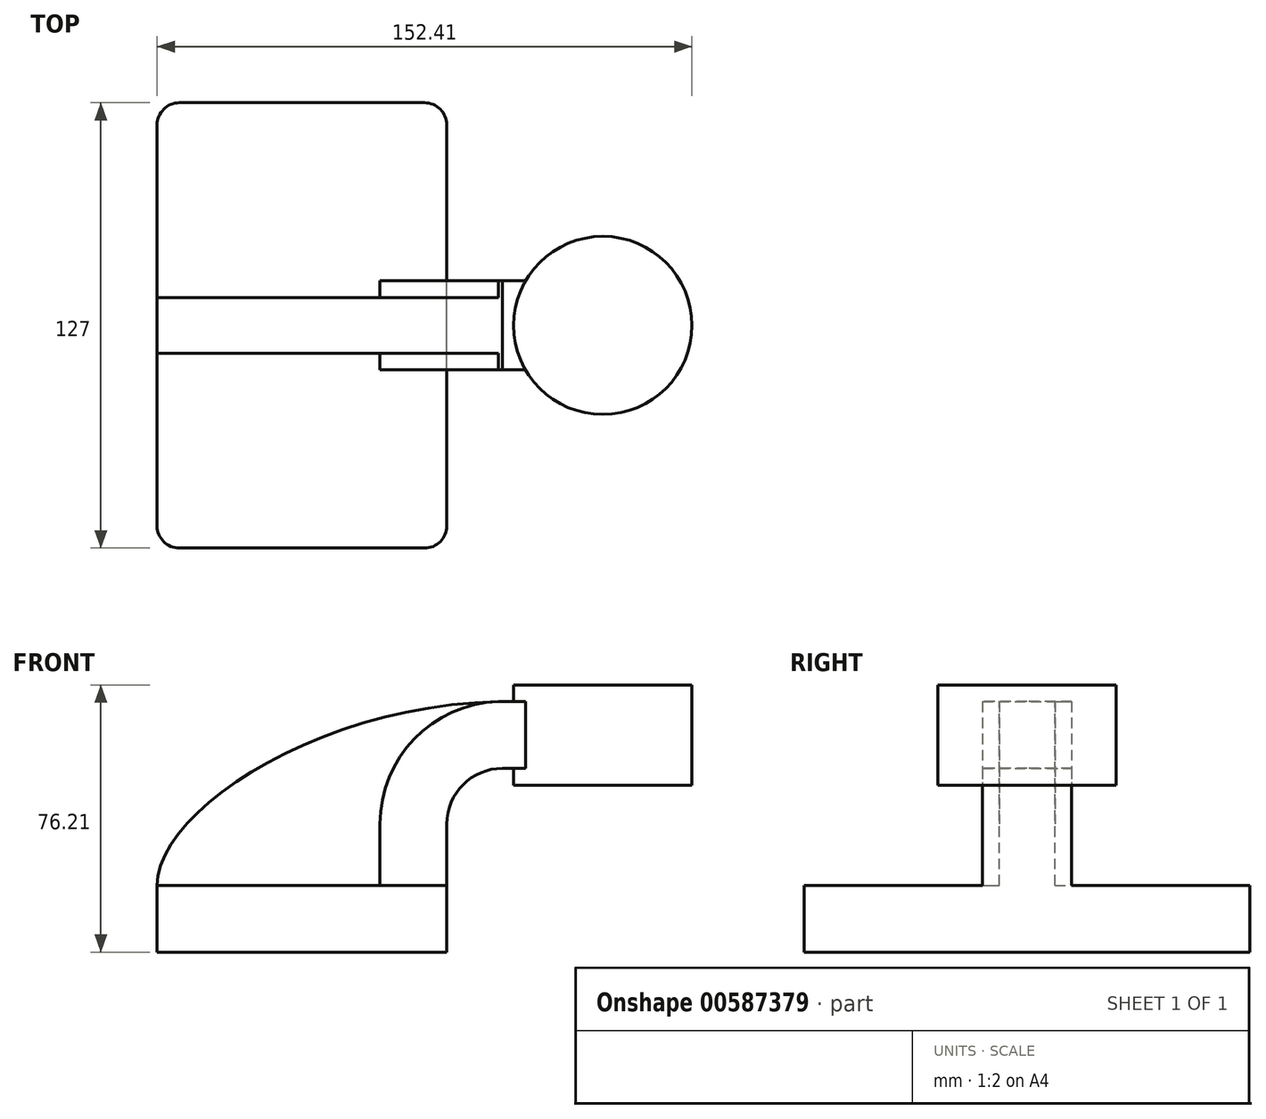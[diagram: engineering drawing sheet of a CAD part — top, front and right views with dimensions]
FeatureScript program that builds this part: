
annotation { "Feature Type Name" : "Feature", "Feature Type Description" : "" }
export const myFeature = defineFeature(function(context is Context, id is Id, definition is map)
    precondition{}
    {
        {
            var Q0;
            Q0=qCreatedBy(makeId("Front.planeOp"),FACE);
            var sketch = newSketch(context, id + "F0", { "sketchPlane" : qUnion([Q0])});
            skLineSegment(sketch, "E0.bottom", {"start": v(41.27, 9.53) * mm, "end": v(-41.28, 9.53) * mm});
            skLineSegment(sketch, "E0.top", {"start": v(41.28, -9.52) * mm, "end": v(-41.27, -9.52) * mm});
            skLineSegment(sketch, "E0.left", {"start": v(41.28, 9.53) * mm, "end": v(41.28, -9.52) * mm});
            skLineSegment(sketch, "E0.right", {"start": v(-41.28, 9.53) * mm, "end": v(-41.28, -9.52) * mm});
            skPoint(sketch, "E0.middle", {"position": v(0, 0) * mm});
            skLineSegment(sketch, "E1.bottom", {"start": v(60.33, 38.1) * mm, "end": v(111.12, 38.1) * mm});
            skLineSegment(sketch, "E1.top", {"start": v(60.32, 66.68) * mm, "end": v(111.12, 66.68) * mm});
            skLineSegment(sketch, "E1.left", {"start": v(60.33, 38.1) * mm, "end": v(60.32, 66.68) * mm});
            skLineSegment(sketch, "E1.right", {"start": v(111.12, 38.1) * mm, "end": v(111.12, 66.68) * mm});
            skLineSegment(sketch, "E2", {"start": v(41.27, 9.53) * mm, "end": v(41.27, 27) * mm});
            skArc(sketch, "E3", {"start": v(41.27, 27) * mm, "mid": v(45.92, 38.23) * mm, "end": v(57.15, 42.88) * mm});
            skLineSegment(sketch, "E4", {"start": v(57.15, 42.88) * mm, "end": v(85.72, 42.88) * mm});
            skPoint(sketch, "E4.endSnap0", {"position": v(85.72, 38.1) * mm});
            skLineSegment(sketch, "E5.0", {"start": v(57.15, 61.93) * mm, "end": v(85.72, 61.93) * mm});
            skArc(sketch, "E5.1", {"start": v(22.22, 27) * mm, "mid": v(32.45, 51.7) * mm, "end": v(57.15, 61.93) * mm});
            skLineSegment(sketch, "E5.2", {"start": v(22.22, 9.53) * mm, "end": v(22.22, 27) * mm});
            skLineSegment(sketch, "E6", {"start": v(85.72, 38.1) * mm, "end": v(85.72, 66.68) * mm});
            skFitSpline(sketch, "E7", {"points": [v(-41.28, 9.52) * mm, v(57.15, 61.93) * mm], "startDerivative": vector(-0.01, 63.76) * mm, "endDerivative": vector(156.94, 2.03) * mm});
            skSolve(sketch);
        }
        {
            var Q0;
            Q0=makeQuery(id+"F0.imprint","IMPRINT",FACE,{"disambiguationData":[TD([[makeQuery(id+"F0.imprint","IMPRINT",EDGE,{"derivedFrom":sQuery(id+"F0.wireOp",EDGE,"E0.top")}),-1.0]])]});
            extrude(context, id + "F1", {"entities" : qUnion([Q0]), "endBound" : BoundingType.SYMMETRIC, "depth" : 127 * mm, "offsetDistance" : 25.4 * mm});
        }
        {
            var Q0;
            {var subQ1=sQuery(id+"F0.wireOp",EDGE,"E2");Q0=makeQuery(id+"F0.imprint","IMPRINT",FACE,{"disambiguationData":[TD([[makeQuery(id+"F0.imprint","IMPRINT",EDGE,{"derivedFrom":subQ1}),1.0]])]});}
            var Q1;
            {var subQ0=sQuery(id+"F0.wireOp",EDGE,"E4");var subQ1=sQuery(id+"F0.wireOp",EDGE,"E1.left");var subQ2=makeQuery(id+"F0.imprint","INTERSECT",VERTEX,{"derivedFrom":[subQ1,subQ0]});Q1=makeQuery(id+"F0.imprint","IMPRINT",FACE,{"disambiguationData":[TD([[makeQuery(id+"F0.imprint","IMPRINT",EDGE,{"disambiguationData":[TD([[subQ2,-1.0]])],"derivedFrom":subQ1}),-1.0]])]});}
            extrude(context, id + "F2", {"entities" : qUnion([Q0, Q1]), "operationType" : NewBodyOperationType.ADD, "endBound" : BoundingType.SYMMETRIC, "depth" : 25.4 * mm, "offsetDistance" : 25.4 * mm});
        }
        {
            var Q0;
            {var subQ3=sQuery(id+"F0.wireOp",EDGE,"E5.2");Q0=makeQuery(id+"F0.imprint","IMPRINT",FACE,{"disambiguationData":[TD([[makeQuery(id+"F0.imprint","IMPRINT",EDGE,{"derivedFrom":subQ3}),1.0]])]});}
            extrude(context, id + "F3", {"entities" : qUnion([Q0]), "operationType" : NewBodyOperationType.ADD, "endBound" : BoundingType.SYMMETRIC, "depth" : 15.88 * mm, "offsetDistance" : 25.4 * mm});
        }
        {
            var Q0;
            {var subQ4=sQuery(id+"F0.wireOp",EDGE,"E1.right");Q0=makeQuery(id+"F0.imprint","IMPRINT",FACE,{"disambiguationData":[TD([[makeQuery(id+"F0.imprint","IMPRINT",EDGE,{"derivedFrom":subQ4}),1.0]])]});}
            var Q1;
            Q1=sQuery(id+"F0.wireOp",EDGE,"E6");
            revolve(context, id + "F4", {"operationType" : NewBodyOperationType.ADD, "entities" : qUnion([Q0]), "axis" : qUnion([Q1]), "revolveType" : RevolveType.FULL});
        }
        {
            var Q0;
            Q0=makeQuery(id+"F1.opExtrude","CAP_EDGE",EDGE,{"disambiguationData":[OSD([sQuery(id+"F0.wireOp",EDGE,"E0.right")])],"isStart":false});
            var Q1;
            Q1=makeQuery(id+"F1.opExtrude","CAP_EDGE",EDGE,{"disambiguationData":[OSD([sQuery(id+"F0.wireOp",EDGE,"E0.left")])],"isStart":false});
            var Q2;
            Q2=makeQuery(id+"F1.opExtrude","CAP_EDGE",EDGE,{"disambiguationData":[OSD([sQuery(id+"F0.wireOp",EDGE,"E0.left")])],"isStart":true});
            var Q3;
            Q3=makeQuery(id+"F1.opExtrude","CAP_EDGE",EDGE,{"disambiguationData":[OSD([sQuery(id+"F0.wireOp",EDGE,"E0.right")])],"isStart":true});
            fillet(context, id + "F5", {"entities" : qUnion([Q0, Q1, Q2, Q3]), "radius" : 6.35 * mm, "tangentPropagation" : true, "allowEdgeOverflow" : false});
        }
    });
